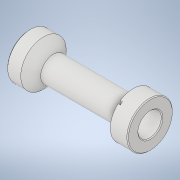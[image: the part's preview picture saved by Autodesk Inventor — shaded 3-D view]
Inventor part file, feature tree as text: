
AUTODESK INVENTOR PART (.ipt)
format: ipt  version: 2020 (Build 240168000, 168)  size: 197,120 bytes
history: native  units: mm
features: sketch x5, projected_geometry x4, plane x3, revolve x2, extrude x2, fillet x2, chamfer x1, mirror x1, pattern_circular x1, hole x1
ambient origin geometry x8: Origin, YZ Plane, XZ Plane, XY Plane, X Axis, Y Axis, Z Axis, Center Point
bodies: Volumenkörper1 (feature_tree)
feature tree (22):
  revolve  "Umdrehung1"
  chamfer  "Fase1"  Distance=2.0mm Angle=45.0deg
  plane  "Arbeitsebene1"
  plane  "Arbeitsebene2"
  extrude  "Extrusion1"  Depth=1.5mm TaperAngle=0.0deg
  mirror  "Spiegeln2"
  fillet  "Rundung1"  Radius=3.0mm
  plane  "Arbeitsebene3"
  sketch  "Skizze3"  dims[d7=90.0deg]
  revolve  "Umdrehung2"
  pattern_circular  "Runde Anordnung1"  [2 undecoded]
  extrude  "Extrusion3"  Depth=2.0mm
  fillet  "Rundung2"  Radius=3.0mm
  hole  "Bohrung1"  [1 undecoded]
  sketch  "Skizze2"  dims[d6=10.8mm]
  projected_geometry  "Projizierte Kontur1"
  projected_geometry  "Projizierte Kontur2"
  projected_geometry  "Projizierte Kontur3"
  projected_geometry  "Projizierte Kontur4"
  sketch  "Skizze4"  dims[d8=21.0mm d9=0.4mm d10=2.0mm d11=45.0deg]
  sketch  "Skizze5"  dims[d12=1.0mm d13=1.5mm d14=0.0mm d15=3.0mm]
  sketch  "Skizze7"  dims[d16=0.1mm d20=-8.6mm d23=7.0mm d24=3.0mm d28=0.5mm d33=55.8mm d34=8.0mm d35=45.0deg d36=36.8mm d37=3.0mm d38=3.490659mm d39=20.0mm d40=360.0deg d42=1.0mm d43=1.0mm d44=0.0mm d45=2.0mm d46=8.0mm d47=2.2mm d48=6.0mm d49=4.0mm d50=2.0mm d51=90.0deg d52=23.5mm d53=90.0deg d54=0.5mm d55=0.872665mm d56=0.5mm d57=0.872665mm]
note: 3 required parameter values undecoded (feature->parameter linkage not recoverable at this tier; creation-order binding heuristic only, values carry confidence <= 0.55)
